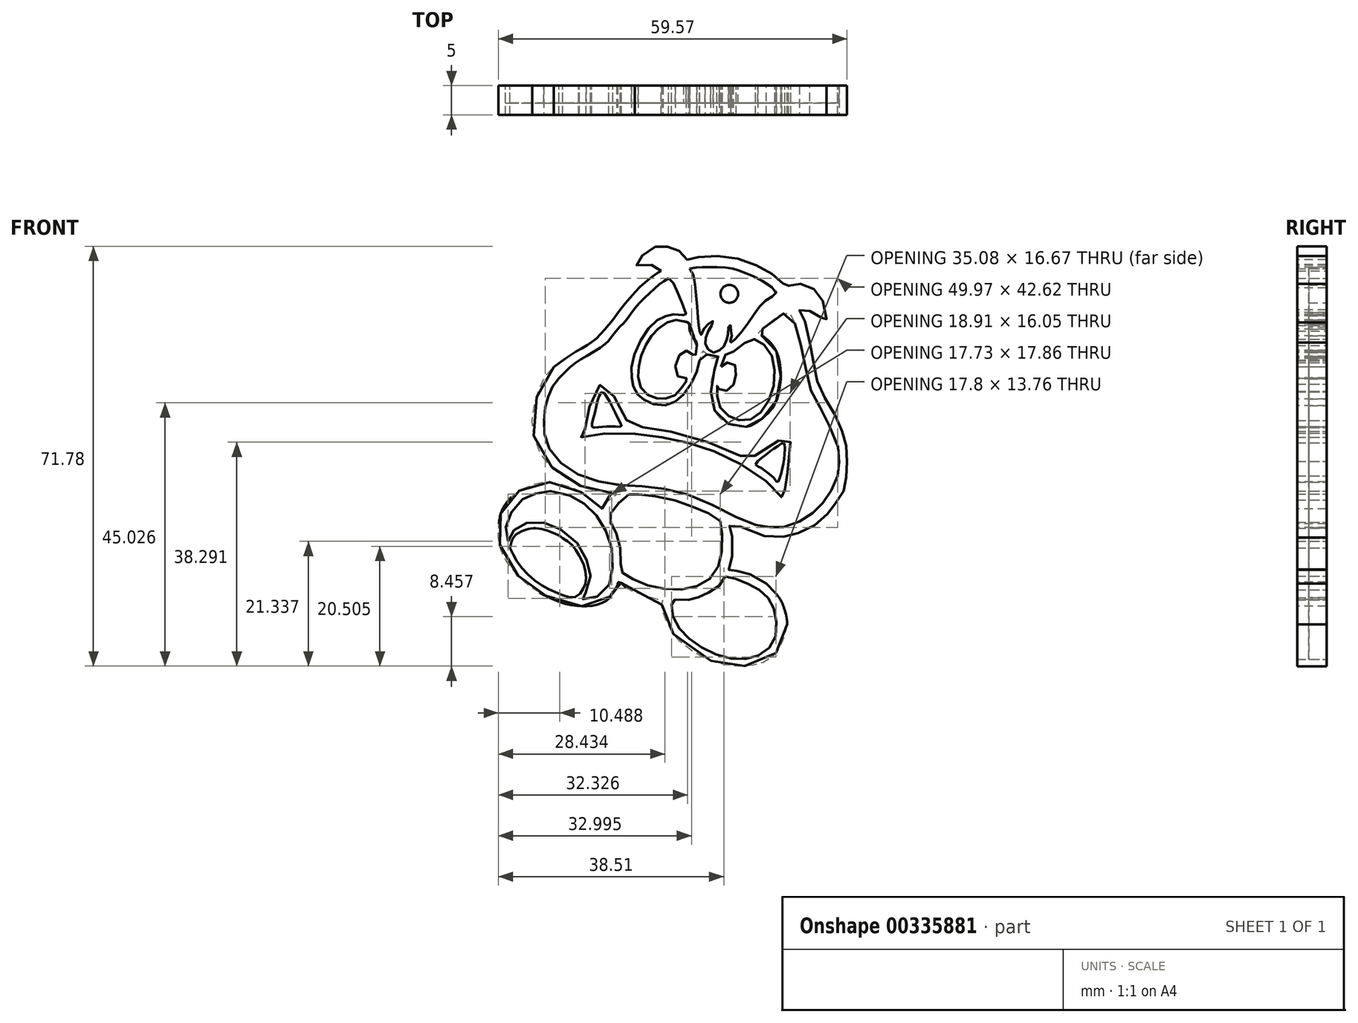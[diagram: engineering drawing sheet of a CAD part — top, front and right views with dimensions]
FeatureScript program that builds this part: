
annotation { "Feature Type Name" : "Feature", "Feature Type Description" : "" }
export const myFeature = defineFeature(function(context is Context, id is Id, definition is map)
    precondition{}
    {
        {
            var Q0;
            Q0=qCreatedBy(makeId("Front.planeOp"),FACE);
            var sketch = newSketch(context, id + "F0", { "sketchPlane" : qUnion([Q0])});
            skFitSpline(sketch, "E0", {"points": [v(-2.97, 28.55) * mm, v(-4.65, 27.43) * mm, v(-6.62, 25.6) * mm, v(-8.8, 23.37) * mm, v(-10.27, 21.27) * mm, v(-11.39, 20.15) * mm, v(-13.07, 18.05) * mm, v(-13.92, 17.21) * mm, v(-16.72, 15.4) * mm, v(-19.18, 13.86) * mm, v(-21.7, 11.48) * mm], "startDerivative": vector(-18.78, -11.26) * mm, "endDerivative": vector(-21.48, -22.08) * mm});
            skFitSpline(sketch, "E1", {"points": [v(-21.7, 11.48) * mm, v(-22.66, 10.25) * mm, v(-23.44, 8.55) * mm, v(-23.97, 7.12) * mm, v(-24.23, 4.77) * mm, v(-24.23, 2.17) * mm, v(-23.05, -1.1) * mm, v(-19.07, -4.69) * mm, v(-12.53, -6.66) * mm, v(-5.88, -7.17) * mm, v(2.05, -9.1) * mm, v(10.68, -13.2) * mm, v(14.07, -14) * mm, v(16.69, -14) * mm, v(20.52, -12.46) * mm, v(22.83, -10.52) * mm, v(24.71, -7.97) * mm, v(26.15, -4.69) * mm], "startDerivative": vector(-26.85, -30.24) * mm, "endDerivative": vector(22.7, 59.84) * mm});
            skFitSpline(sketch, "E2", {"points": [v(25.72, -5.82) * mm, v(26.15, -4.37) * mm, v(26.15, -2.72) * mm, v(26.15, -1.14) * mm, v(24.97, 2.22) * mm, v(23.34, 5.7) * mm, v(21.82, 8.23) * mm, v(20.71, 11.84) * mm, v(19.8, 16.4) * mm, v(18.75, 20.24) * mm, v(17.48, 22.65) * mm, v(13.51, 20.22) * mm, v(12.3, 19) * mm, v(13.08, 18.66) * mm, v(15.52, 15.87) * mm, v(16.13, 10.65) * mm, v(14.73, 6.3) * mm, v(11.77, 3.7) * mm, v(9.85, 3.1) * mm, v(7.06, 3.7) * mm, v(4.97, 5.8) * mm, v(4.27, 8.66) * mm, v(4.62, 12.14) * mm, v(5.67, 15.18) * mm, v(5.06, 14.92) * mm, v(4.01, 15.01) * mm, v(2.88, 16.06) * mm, v(2.18, 12.84) * mm], "startDerivative": vector(20.24, 51.46) * mm, "endDerivative": vector(-10.26, -118.99) * mm});
            skFitSpline(sketch, "E3", {"points": [v(2.32, 14.44) * mm, v(1.54, 11.78) * mm, v(-0.5, 8.62) * mm, v(-2.36, 7.16) * mm, v(-4.84, 6.82) * mm, v(-7.1, 7.73) * mm, v(-8.23, 8.63) * mm, v(-9.02, 10.21) * mm, v(-9.3, 11.8) * mm, v(-9.14, 14.44) * mm, v(-7.33, 18.69) * mm, v(-5.1, 21.24) * mm, v(-3.4, 22.08) * mm, v(-2.22, 22.38) * mm, v(-0.36, 22.2) * mm, v(0, 22.12) * mm, v(-0.45, 23.77) * mm, v(-1.72, 26.81) * mm, v(-2.22, 27.83) * mm, v(-2.97, 28.55) * mm], "startDerivative": vector(-8.88, -42.44) * mm, "endDerivative": vector(-22.19, 18.63) * mm});
            skLineSegment(sketch, "E4", {"start": v(2.32, 14.44) * mm, "end": v(2.35, 14.58) * mm});
            skFitSpline(sketch, "E5", {"points": [v(0.63, 30.2) * mm, v(1.28, 29.07) * mm, v(1.55, 27.14) * mm, v(1.87, 24.24) * mm, v(2.08, 21.67) * mm, v(2.19, 20.38) * mm, v(2.35, 19.3) * mm, v(2.56, 18.66) * mm, v(2.73, 19.47) * mm, v(3.2, 20.06) * mm, v(3.85, 20.76) * mm, v(4.55, 21.24) * mm, v(4.66, 20.8) * mm, v(4.28, 20.38) * mm, v(3.8, 19.52) * mm, v(3.37, 18.45) * mm, v(3.26, 17.6) * mm, v(3.58, 16.63) * mm, v(4.12, 16.1) * mm, v(4.87, 15.82) * mm, v(5.73, 16.2) * mm, v(6.37, 16.73) * mm, v(6.8, 17.6) * mm, v(7.02, 18.45) * mm, v(7.23, 19.25) * mm, v(7.23, 20.27) * mm, v(7.28, 20.49) * mm, v(7.55, 20.54) * mm, v(7.66, 19.9) * mm, v(7.87, 18.99) * mm], "startDerivative": vector(18.48, -25.71) * mm, "endDerivative": vector(8.27, -25.56) * mm});
            skPoint(sketch, "E6.1.internal.orphan", {"position": v(7.78, 18.33) * mm});
            skFitSpline(sketch, "E7", {"points": [v(7.55, 20.54) * mm, v(7.72, 19.51) * mm, v(7.78, 18.5) * mm, v(7.55, 17.57) * mm, v(7.66, 17.55) * mm, v(8.6, 18.33) * mm, v(11.7, 22.48) * mm, v(13.95, 24.97) * mm, v(15.4, 26.06) * mm, v(12.3, 28.47) * mm, v(9.46, 29.71) * mm, v(7.55, 30.28) * mm, v(4.72, 30.44) * mm, v(2.47, 30.44) * mm, v(0.63, 30.2) * mm], "startDerivative": vector(3.05, -20.12) * mm, "endDerivative": vector(-26, -4.4) * mm});
            skFitSpline(sketch, "E8", {"points": [v(-17.27, 2.73) * mm, v(-16.97, 4.68) * mm, v(-16.27, 7.12) * mm, v(-15.07, 9.87) * mm, v(-14.37, 10.42) * mm, v(-13.38, 9.92) * mm, v(-11.78, 7.42) * mm, v(-10.38, 4.88) * mm, v(-9.58, 3.08) * mm, v(-8.8, 3.16) * mm, v(-3.97, 2.38) * mm, v(-2.42, 2.3) * mm, v(3.8, 0.48) * mm, v(8.8, -1.5) * mm, v(11.05, -2.8) * mm, v(11.31, -2.41) * mm, v(13.21, -0.68) * mm, v(15.97, 0.87) * mm, v(16.67, 1.22) * mm, v(17.53, 1.26) * mm, v(17.87, -1.16) * mm, v(17.18, -5.22) * mm, v(16.4, -7.12) * mm, v(16.57, -7.3) * mm, v(17.55, -8.7) * mm, v(17.13, -9.36) * mm, v(15.93, -8.47) * mm, v(14.54, -6.98) * mm, v(12.59, -5.27) * mm, v(8.97, -3.04) * mm, v(5.49, -1.37) * mm, v(2.84, -0.35) * mm, v(-0.68, 0.67) * mm, v(-3.6, 1.23) * mm, v(-6.44, 1.79) * mm, v(-9.6, 1.97) * mm, v(-13.68, 2.02) * mm, v(-16.46, 1.7) * mm, v(-18.09, 1.42) * mm, v(-18.32, 1.88) * mm, v(-18.04, 2.44) * mm, v(-17.27, 2.73) * mm]});
            skFitSpline(sketch, "E9", {"points": [v(-16.09, 3.15) * mm, v(-15.71, 5) * mm, v(-15.16, 7.42) * mm, v(-14.32, 9.09) * mm, v(-13.3, 7.88) * mm, v(-12, 5.37) * mm, v(-11.07, 3.43) * mm, v(-11.07, 3.2) * mm, v(-12.56, 3.2) * mm, v(-14.04, 3.15) * mm, v(-15.44, 3.05) * mm, v(-16.09, 3.15) * mm]});
            skFitSpline(sketch, "E10", {"points": [v(11.87, -3.32) * mm, v(13.36, -1.87) * mm, v(14.46, -0.96) * mm, v(15.5, -0.31) * mm, v(16.7, 0.4) * mm, v(16.85, -0.96) * mm, v(16.72, -2.55) * mm, v(16.4, -4.23) * mm, v(15.95, -5.78) * mm, v(15.62, -6.33) * mm, v(15.14, -5.75) * mm, v(13.42, -4.32) * mm, v(12.55, -3.74) * mm, v(11.87, -3.32) * mm]});
            skFitSpline(sketch, "E11", {"points": [v(-0.45, 21.2) * mm, v(-1.35, 21.4) * mm, v(-2.45, 21.3) * mm, v(-4, 20.54) * mm, v(-5.44, 19.2) * mm, v(-6.24, 18.2) * mm, v(-7.33, 16.15) * mm, v(-7.93, 14.2) * mm, v(-8.18, 12.51) * mm, v(-7.93, 10.52) * mm, v(-7.1, 9.02) * mm, v(-5.54, 8.17) * mm, v(-4.5, 7.94) * mm, v(-3.08, 8) * mm, v(-1.6, 8.79) * mm, v(-0.7, 9.9) * mm, v(-0.08, 10.73) * mm, v(0.4, 11.48) * mm, v(-0.29, 11.36) * mm, v(-1.45, 11.87) * mm, v(-1.8, 13.64) * mm, v(-0.95, 15.57) * mm, v(0, 16.13) * mm, v(0.76, 16.06) * mm, v(1.55, 14.94) * mm, v(1.7, 15.81) * mm, v(1.83, 17.03) * mm, v(1.31, 18.18) * mm, v(0.58, 19.95) * mm, v(0.58, 20.82) * mm, v(-0.45, 21.2) * mm]});
            skFitSpline(sketch, "E12", {"points": [v(0.58, 19.95) * mm, v(0.45, 20.78) * mm, v(-0.45, 21.2) * mm], "startDerivative": vector(0.09, 1.96) * mm, "endDerivative": vector(-2.12, 0.54) * mm});
            skFitSpline(sketch, "E13", {"points": [v(0.45, 20.78) * mm, v(0.77, 20.17) * mm, v(1.18, 18.97) * mm, v(1.52, 18.09) * mm, v(1.82, 17.46) * mm, v(1.83, 17.03) * mm], "startDerivative": vector(1.64, -2.91) * mm, "endDerivative": vector(-0.3, -2.83) * mm});
            skFitSpline(sketch, "E14", {"points": [v(6, 13.4) * mm, v(6.7, 15.44) * mm, v(7.38, 15.7) * mm, v(9.2, 16.73) * mm, v(10.84, 18.03) * mm, v(12.04, 18.03) * mm, v(13.51, 17) * mm, v(14.8, 14.94) * mm, v(15.15, 12.14) * mm, v(14.68, 8.96) * mm, v(13.34, 6.37) * mm, v(11.74, 4.73) * mm, v(10.14, 4.25) * mm, v(8.29, 4.43) * mm, v(6.86, 5.33) * mm, v(5.65, 6.72) * mm, v(5.3, 8.44) * mm, v(5.3, 9.9) * mm, v(5.4, 10.43) * mm, v(5.57, 9.65) * mm, v(6.26, 9.26) * mm, v(7.2, 9.4) * mm, v(8.07, 10.26) * mm, v(8.42, 11.55) * mm, v(8.6, 12.72) * mm, v(8.24, 13.88) * mm, v(7.2, 14.14) * mm, v(6.52, 13.88) * mm, v(6, 13.4) * mm]});
            skPoint(sketch, "E15.7.internal.snap0", {"position": v(-2.23, 33.94) * mm});
            skFitSpline(sketch, "E15", {"points": [v(-4.24, 29.8) * mm, v(-5.42, 30.62) * mm, v(-6.85, 30.86) * mm, v(-8.74, 30.86) * mm, v(-6.76, 33) * mm, v(-5.04, 33.94) * mm, v(-3.48, 33.94) * mm, v(-2.23, 33.72) * mm, v(-0.5, 32.64) * mm, v(0.22, 31.74) * mm, v(0.83, 31.92) * mm, v(3.5, 32.28) * mm, v(7.69, 32.15) * mm, v(11.63, 30.9) * mm, v(14.57, 29.35) * mm, v(16.42, 27.9) * mm, v(17.02, 26.86) * mm, v(17.57, 27.26) * mm, v(18.96, 27.56) * mm, v(20.86, 27.3) * mm, v(22.65, 25.86) * mm, v(23.75, 23.52) * mm, v(23.95, 20.97) * mm, v(23.15, 21.77) * mm, v(21.46, 22.87) * mm, v(20.16, 23.07) * mm, v(19.36, 23.07) * mm, v(20.02, 21.91) * mm, v(21.18, 17.53) * mm, v(22.56, 12) * mm, v(22.93, 10.1) * mm], "startDerivative": vector(-41.87, 33.38) * mm, "endDerivative": vector(8.31, -49.64) * mm});
            skFitSpline(sketch, "E16", {"points": [v(21.18, 17.53) * mm, v(21.97, 13.17) * mm, v(23, 9.38) * mm, v(25.14, 5.71) * mm, v(26.67, 2.4) * mm, v(27.37, 0) * mm, v(27.51, -2.8) * mm, v(27.36, -5.57) * mm, v(27.03, -7.66) * mm, v(25.42, -10.13) * mm, v(24.49, -11.4) * mm, v(22.56, -13.27) * mm, v(19.25, -15.02) * mm, v(16.71, -15.66) * mm, v(12.38, -15.28) * mm, v(7.6, -13.45) * mm, v(7.45, -14) * mm, v(7.78, -14.99) * mm, v(7.9, -18.87) * mm, v(7.3, -21.3) * mm, v(7.74, -21.26) * mm, v(8.68, -21.52) * mm, v(10.44, -21.9) * mm, v(13.72, -23.7) * mm, v(15.52, -25.3) * mm, v(16.33, -25.19) * mm], "startDerivative": vector(15.03, -83.6) * mm, "endDerivative": vector(34.66, 13.88) * mm});
            skFitSpline(sketch, "E17", {"points": [v(13.72, -23.7) * mm, v(15.33, -25.35) * mm, v(16.11, -26.36) * mm, v(16.55, -27.28) * mm, v(16.93, -28.4) * mm, v(17.29, -30.63) * mm, v(16.41, -34.42) * mm, v(13.72, -37.27) * mm], "startDerivative": vector(11.67, -11.78) * mm, "endDerivative": vector(-15.83, -13.1) * mm});
            skFitSpline(sketch, "E18", {"points": [v(17.29, -30.63) * mm, v(16.73, -32.78) * mm, v(15.75, -34.97) * mm, v(13.7, -36.93) * mm, v(10.72, -37.71) * mm, v(8.56, -37.78) * mm, v(5.65, -37.33) * mm, v(1.22, -35.3) * mm, v(-2.5, -31.78) * mm, v(-3.75, -29) * mm, v(-4.17, -27.42) * mm, v(-3.93, -26.45) * mm, v(-4.54, -26.4) * mm, v(-6.95, -25.75) * mm, v(-8.62, -25.2) * mm, v(-10.3, -24.36) * mm, v(-11.24, -23.47) * mm, v(-11.63, -23.47) * mm, v(-11.69, -24.07) * mm, v(-12.6, -25.24) * mm, v(-13.17, -26.22) * mm, v(-15.4, -27.34) * mm, v(-18.1, -27.52) * mm, v(-21.25, -26.92) * mm, v(-24.5, -25.48) * mm, v(-26.55, -24.2) * mm, v(-29.15, -21.8) * mm, v(-31.14, -19) * mm, v(-31.93, -16.57) * mm, v(-32.04, -14.5) * mm, v(-31.65, -11.68) * mm, v(-30.6, -9.73) * mm, v(-29.18, -8.24) * mm, v(-26.79, -6.97) * mm, v(-24.62, -6.3) * mm, v(-21.9, -6.52) * mm, v(-19.24, -7.34) * mm, v(-16.96, -8.61) * mm, v(-15.13, -10.15) * mm, v(-14.46, -10.93) * mm, v(-13.78, -9.88) * mm, v(-11.84, -8.39) * mm, v(-12.66, -8.16) * mm, v(-15.17, -7.87) * mm, v(-17.37, -7.27) * mm, v(-19.99, -5.92) * mm, v(-22.23, -4.35) * mm, v(-24.23, -2.4) * mm, v(-25.78, 0.83) * mm, v(-26.28, 4.7) * mm, v(-25.5, 8.27) * mm, v(-24.23, 11.56) * mm, v(-22.56, 13.35) * mm, v(-19.18, 15.36) * mm], "startDerivative": vector(-27.45, -117.84) * mm, "endDerivative": vector(152.33, 82.57) * mm});
            skFitSpline(sketch, "E19", {"points": [v(-22.56, 13.35) * mm, v(-20.19, 15.09) * mm, v(-17.86, 16.54) * mm, v(-15.83, 17.8) * mm, v(-14.33, 19.3) * mm, v(-12.69, 21.2) * mm, v(-10.97, 23.48) * mm, v(-8.65, 26.24) * mm, v(-6.56, 28.18) * mm, v(-5.07, 29.3) * mm, v(-4.24, 29.8) * mm], "startDerivative": vector(21.5, 16.2) * mm, "endDerivative": vector(12.42, 6.83) * mm});
            skFitSpline(sketch, "E20", {"points": [v(6.67, -22.45) * mm, v(8.46, -22.82) * mm, v(11.13, -23.94) * mm, v(13.11, -25.24) * mm, v(14.6, -26.91) * mm, v(15.33, -29.37) * mm, v(15.33, -32.6) * mm, v(13.93, -34.91) * mm, v(11.37, -36.32) * mm, v(8.64, -36.57) * mm, v(5, -35.74) * mm, v(1.45, -33.76) * mm, v(-0.95, -31.6) * mm, v(-2.27, -29.13) * mm, v(-2.44, -26.98) * mm, v(-2.27, -26.48) * mm, v(0, -26.48) * mm, v(1.78, -26.15) * mm, v(3.51, -25.35) * mm, v(5.66, -24.08) * mm, v(6.67, -22.45) * mm]});
            skFitSpline(sketch, "E21", {"points": [v(-30.06, -17.55) * mm, v(-29.4, -15.65) * mm, v(-27.74, -14.57) * mm, v(-26.42, -14.24) * mm, v(-24.68, -14.32) * mm, v(-22.78, -14.99) * mm, v(-21.04, -15.9) * mm, v(-19.47, -17.71) * mm], "startDerivative": vector(2.58, 14.16) * mm, "endDerivative": vector(9.26, -12.71) * mm});
            skFitSpline(sketch, "E22", {"points": [v(-21.04, -15.9) * mm, v(-19.47, -17.04) * mm, v(-18.2, -18.98) * mm, v(-17.46, -20.56) * mm, v(-17.1, -23.07) * mm, v(-17.65, -24.74) * mm, v(-19.09, -26.04) * mm, v(-21.87, -25.35) * mm, v(-24.89, -23.8) * mm, v(-28.41, -20.56) * mm, v(-30.06, -17.55) * mm], "startDerivative": vector(19.14, -11.06) * mm, "endDerivative": vector(-11.39, 26.06) * mm});
            skFitSpline(sketch, "E23", {"points": [v(-30.42, -16.42) * mm, v(-30.2, -15.58) * mm, v(-29.38, -14.5) * mm, v(-28.24, -13.63) * mm, v(-26.44, -13.19) * mm, v(-24.49, -13.24) * mm, v(-22.77, -13.6) * mm, v(-19.8, -15.64) * mm, v(-18.1, -17.46) * mm, v(-16.96, -19.73) * mm, v(-16.4, -21.24) * mm, v(-16.48, -23.87) * mm, v(-17.3, -25.38) * mm, v(-18.19, -26.22) * mm, v(-17.57, -26.33) * mm, v(-16.26, -26.3) * mm, v(-14.6, -25.5) * mm, v(-13.26, -24.1) * mm, v(-12.65, -22.16) * mm, v(-12.53, -19.67) * mm, v(-12.8, -17.13) * mm, v(-13.63, -14.94) * mm, v(-14.4, -13.24) * mm, v(-16.1, -11.2) * mm, v(-17.36, -10.05) * mm, v(-19.04, -9.07) * mm, v(-20.83, -8.26) * mm, v(-23.8, -7.86) * mm, v(-25.2, -8.14) * mm, v(-26.43, -8.54) * mm, v(-27.66, -9.04) * mm, v(-29.34, -10.8) * mm, v(-30.07, -11.81) * mm, v(-30.68, -13.52) * mm, v(-30.8, -15.7) * mm, v(-30.42, -16.42) * mm]});
            skFitSpline(sketch, "E24", {"points": [v(-9.75, -8.43) * mm, v(-11.4, -9.82) * mm, v(-12.7, -11.43) * mm, v(-13.18, -12.72) * mm, v(-12.54, -13.58) * mm, v(-11.57, -16.47) * mm, v(-11.03, -19.15) * mm, v(-11.2, -21.67) * mm, v(-10.6, -21.89) * mm, v(-8.67, -23.17) * mm, v(-5.46, -24.25) * mm, v(-1.97, -24.73) * mm, v(1.4, -24.25) * mm, v(3.98, -22.9) * mm, v(5.59, -20.55) * mm, v(6.18, -17.55) * mm, v(6.12, -14.11) * mm, v(5.53, -12.61) * mm, v(2.53, -11.11) * mm, v(-1.17, -9.66) * mm, v(-6.1, -8.65) * mm, v(-8.67, -8.38) * mm, v(-9.75, -8.43) * mm]});
            skCircle(sketch, "E25", {"center": v(7.4, 25.87) * mm, "radius": 1.52 * mm});
            skSolve(sketch);
        }
        {
            var Q0;
            Q0=makeQuery(id+"F0.imprint","IMPRINT",FACE,{"disambiguationData":[TD([[makeQuery(id+"F0.imprint","IMPRINT",EDGE,{"derivedFrom":sQuery(id+"F0.wireOp",EDGE,"E0")}),-1.0]])]});
            var Q1;
            Q1=makeQuery(id+"F0.imprint","IMPRINT",FACE,{"disambiguationData":[TD([[makeQuery(id+"F0.imprint","IMPRINT",EDGE,{"derivedFrom":sQuery(id+"F0.wireOp",EDGE,"E8")}),-1.0]])]});
            extrude(context, id + "F1", {"entities" : qUnion([Q0, Q1]), "depth" : 5 * mm});
        }
        {
            var Q0;
            Q0=makeQuery(id+"F0.imprint","IMPRINT",FACE,{"disambiguationData":[TD([[makeQuery(id+"F0.imprint","IMPRINT",EDGE,{"derivedFrom":sQuery(id+"F0.wireOp",EDGE,"E0")}),1.0]])]});
            var Q1;
            {var subQ0=sQuery(id+"F0.wireOp",EDGE,"E7");var subQ1=sQuery(id+"F0.wireOp",EDGE,"E5");var subQ2=makeQuery(id+"F0.imprint","INTERSECT",VERTEX,{"disambiguationData":[OD(0.0)],"derivedFrom":[subQ1,subQ0]});Q1=makeQuery(id+"F0.imprint","IMPRINT",FACE,{"disambiguationData":[TD([[makeQuery(id+"F0.imprint","IMPRINT",EDGE,{"disambiguationData":[TD([[subQ2,-1.0]])],"derivedFrom":subQ1}),1.0]])]});}
            var Q2;
            {var subQ0=sQuery(id+"F0.wireOp",EDGE,"E11");Q2=makeQuery(id+"F0.imprint","IMPRINT",FACE,{"disambiguationData":[TD([[makeQuery(id+"F0.imprint","IMPRINT",EDGE,{"derivedFrom":subQ0}),1.0]])]});}
            var Q3;
            Q3=makeQuery(id+"F0.imprint","IMPRINT",FACE,{"disambiguationData":[TD([[makeQuery(id+"F0.imprint","IMPRINT",EDGE,{"derivedFrom":sQuery(id+"F0.wireOp",EDGE,"E14")}),-1.0]])]});
            var Q4;
            Q4=makeQuery(id+"F0.imprint","IMPRINT",FACE,{"disambiguationData":[TD([[makeQuery(id+"F0.imprint","IMPRINT",EDGE,{"derivedFrom":sQuery(id+"F0.wireOp",EDGE,"E10")}),-1.0]])]});
            var Q5;
            Q5=makeQuery(id+"F0.imprint","IMPRINT",FACE,{"disambiguationData":[TD([[makeQuery(id+"F0.imprint","IMPRINT",EDGE,{"derivedFrom":sQuery(id+"F0.wireOp",EDGE,"E9")}),-1.0]])]});
            var Q6;
            Q6=makeQuery(id+"F0.imprint","IMPRINT",FACE,{"disambiguationData":[TD([[makeQuery(id+"F0.imprint","IMPRINT",EDGE,{"derivedFrom":sQuery(id+"F0.wireOp",EDGE,"E24")}),1.0]])]});
            var Q7;
            Q7=makeQuery(id+"F0.imprint","IMPRINT",FACE,{"disambiguationData":[TD([[makeQuery(id+"F0.imprint","IMPRINT",EDGE,{"derivedFrom":sQuery(id+"F0.wireOp",EDGE,"E23")}),1.0]])]});
            var Q8;
            Q8=makeQuery(id+"F0.imprint","IMPRINT",FACE,{"disambiguationData":[TD([[makeQuery(id+"F0.imprint","IMPRINT",EDGE,{"derivedFrom":sQuery(id+"F0.wireOp",EDGE,"E21")}),-1.0]])]});
            var Q9;
            Q9=makeQuery(id+"F0.imprint","IMPRINT",FACE,{"disambiguationData":[TD([[makeQuery(id+"F0.imprint","IMPRINT",EDGE,{"derivedFrom":sQuery(id+"F0.wireOp",EDGE,"E20")}),-1.0]])]});
            extrude(context, id + "F2", {"entities" : qUnion([Q0, Q1, Q2, Q3, Q4, Q5, Q6, Q7, Q8, Q9]), "depth" : 3 * mm});
        }
        {
            var Q0;
            Q0=sQuery(id+"F0.wireOp",VERTEX,"E25.center");
            var Q1;
            Q1=makeQuery(id+"F1.opExtrude","SWEPT_BODY",BODY,{"disambiguationData":[OSD([sQuery(id+"F0.wireOp",EDGE,"E0"),sQuery(id+"F0.wireOp",EDGE,"E1"),sQuery(id+"F0.wireOp",EDGE,"E2"),sQuery(id+"F0.wireOp",EDGE,"E3"),sQuery(id+"F0.wireOp",EDGE,"E4"),sQuery(id+"F0.wireOp",EDGE,"E5"),sQuery(id+"F0.wireOp",EDGE,"E7"),sQuery(id+"F0.wireOp",EDGE,"E11"),sQuery(id+"F0.wireOp",EDGE,"E12"),sQuery(id+"F0.wireOp",EDGE,"E13"),sQuery(id+"F0.wireOp",EDGE,"E14"),sQuery(id+"F0.wireOp",EDGE,"E15"),sQuery(id+"F0.wireOp",EDGE,"E16"),sQuery(id+"F0.wireOp",EDGE,"E17"),sQuery(id+"F0.wireOp",EDGE,"E18"),sQuery(id+"F0.wireOp",EDGE,"E19"),sQuery(id+"F0.wireOp",EDGE,"E20"),sQuery(id+"F0.wireOp",EDGE,"E21"),sQuery(id+"F0.wireOp",EDGE,"E22"),sQuery(id+"F0.wireOp",EDGE,"E23"),sQuery(id+"F0.wireOp",EDGE,"E24")])]});
            hole(context, id + "F3", {"style" : HoleStyle.SIMPLE, "endStyle" : HoleEndStyle.THROUGH, "oppositeDirection" : true, "holeDiameter" : 5 * mm, "isTappedThrough" : true, "tappedDepth" : 12 * mm, "tapClearance" : 3, "locations" : qUnion([Q0]), "scope" : qUnion([Q1])});
        }
    });
